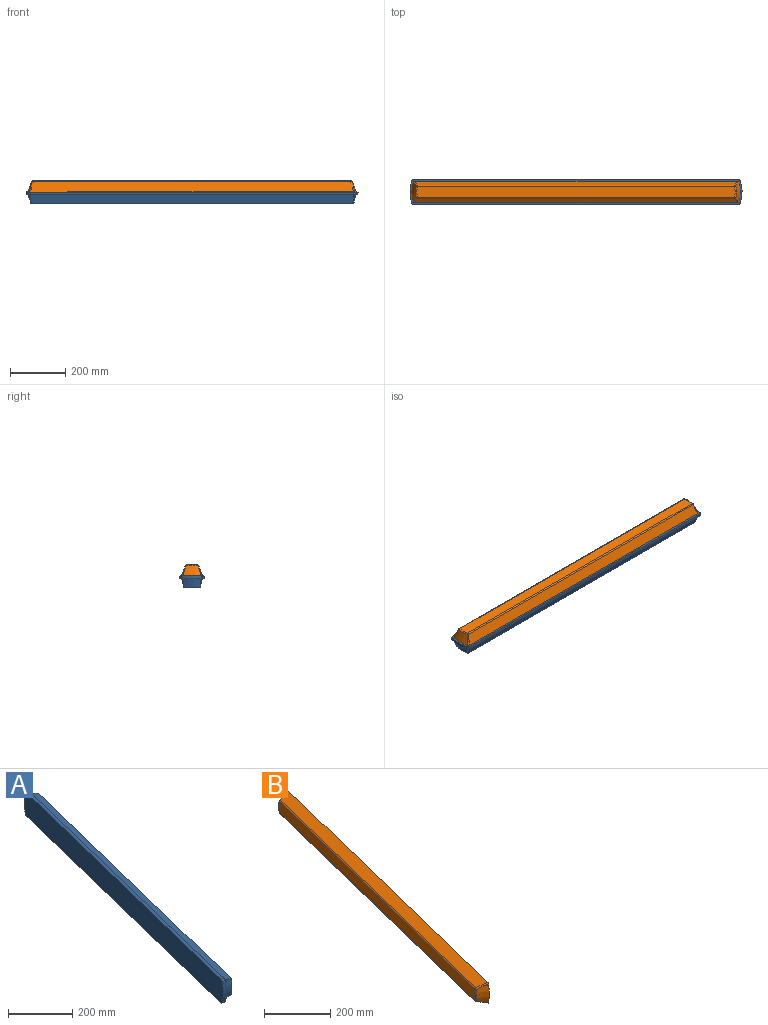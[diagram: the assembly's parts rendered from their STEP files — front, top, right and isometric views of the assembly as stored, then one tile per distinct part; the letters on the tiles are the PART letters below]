
ASSEMBLY  parts=2 mates=1
PART A: 27 faces, bbox 325.7x1167.6x90 mm
  f0: plane 1165.2x290.52mm, normal (0.97,-0.24,0), area 17663.3mm2, adj f1,f2,f3,f4,f5,f6,f7,f8
  f1: cylinder r=10mm len=12.04mm, axis (-0.97,0.24,0), area 130.5mm2, adj f0,f2,f12,f13
  f2: plane 10.02x4.74mm, normal (0.23,0.94,-0.26), area 49.1mm2, adj f0,f1,f3,f13
  f3: cylinder r=125mm len=65.78mm, axis (-0.97,0.24,0), area 665.7mm2, adj f0,f2,f4,f13
  f4: plane 10.02x4.74mm, normal (0.23,0.94,0.26), area 49.1mm2, adj f0,f3,f5,f13
  f5: cylinder r=10mm len=12.04mm, axis (-0.97,0.24,0), area 130.5mm2, adj f0,f4,f6,f13
  f6: plane 1137.84x292.79mm, normal (0,0,1), area 11701.8mm2, adj f0,f5,f7,f13
  f7: cylinder r=10mm len=12.04mm, axis (-0.97,0.24,0), area 130.5mm2, adj f0,f6,f8,f13
  f8: plane 10.02x4.74mm, normal (-0.23,-0.94,0.26), area 49.1mm2, adj f0,f7,f9,f13
  f9: cylinder r=125mm len=65.78mm, axis (-0.97,0.24,0), area 665.7mm2, adj f0,f8,f10,f13
  f10: plane 10.02x4.74mm, normal (-0.23,-0.94,-0.26), area 49.1mm2, adj f0,f9,f11,f13
  f11: cylinder r=10mm len=12.04mm, axis (-0.97,0.24,0), area 130.5mm2, adj f0,f10,f12,f13
  f12: plane 1137.84x292.79mm, normal (0,0,-1), area 11701.8mm2, adj f0,f1,f11,f13
  f13: plane 1165.2x290.52mm, normal (-0.97,0.24,0), area 107548.4mm2, adj f1,f2,f3,f4,f5,f6,f7,f8
  f14: plane 1138.94x311.27mm, normal (0.25,-0.06,-0.97), area 36268.8mm2, adj f0,f15,f16,f24,f25,f26
  f15: cone r=0.3mm half-angle=15deg, axis (-0.97,0.24,0), area 22.7mm2, adj f0,f14,f16
  f16: plane 27.55x15.05mm, normal (0.48,0.84,-0.25), area 115.1mm2, adj f0,f14,f15,f17,f26
  f17: cone r=110.77mm half-angle=15deg, axis (-0.97,0.24,0), area 1885.2mm2, adj f0,f16,f18,f26
  f18: plane 27.55x15.05mm, normal (0.48,0.84,0.25), area 115.1mm2, adj f0,f17,f19,f20,f26
  f19: cone r=0.3mm half-angle=15deg, axis (-0.97,0.24,0), area 22.7mm2, adj f0,f18,f20
  f20: plane 1138.94x311.27mm, normal (0.25,-0.06,0.97), area 36268.8mm2, adj f0,f18,f19,f21,f22,f26
  f21: cone r=0.3mm half-angle=15deg, axis (-0.97,0.24,0), area 22.7mm2, adj f0,f20,f22
  f22: plane 31.05x6.85mm, normal (0.03,-0.97,0.25), area 115.1mm2, adj f0,f20,f21,f23,f26
  f23: cone r=110.77mm half-angle=15deg, axis (-0.97,0.24,0), area 1885.2mm2, adj f0,f22,f24,f26
  f24: plane 31.05x6.85mm, normal (0.03,-0.97,-0.25), area 115.1mm2, adj f0,f14,f23,f25,f26
  f25: cone r=0.3mm half-angle=15deg, axis (-0.97,0.24,0), area 22.7mm2, adj f0,f14,f24
  f26: plane 1136.01x283.24mm, normal (0.97,-0.24,0), area 69992.4mm2, adj f14,f16,f17,f18,f20,f22,f23,f24
PART B: 26 faces, bbox 324.4x1156.6x76.8 mm
  f0: sphere r=5mm, area 17.3mm2, adj f8,f11,f13
  f1: sphere r=5mm, area 17.3mm2, adj f6,f10,f11
  f2: sphere r=5mm, area 17.3mm2, adj f4,f7,f8
  f3: sphere r=5mm, area 17.3mm2, adj f4,f5,f6
  f4: cylinder r=5mm len=1113.46mm, axis (0.24,0.97,0), area 7005mm2, adj f2,f3,f21,f22
  f5: bspline ~25.75x12.39mm, area 162.6mm2, adj f3,f9,f22,f24
  f6: torus R=99.94mm, axis (0.97,-0.24,0), area 251.9mm2, adj f1,f3,f21,f24
  f7: bspline ~22.68x16.74mm, area 162.6mm2, adj f2,f12,f17,f22
  f8: torus R=99.94mm, axis (0.97,-0.24,0), area 251.9mm2, adj f0,f2,f17,f21
  f9: cylinder r=5mm len=14.59mm, axis (0.94,0.03,-0.33), area 86.8mm2, adj f5,f20,f22,f25
  f10: bspline ~25.75x12.39mm, area 162.6mm2, adj f1,f14,f19,f24
  f11: cylinder r=5mm len=1113.46mm, axis (-0.24,-0.97,0), area 7005mm2, adj f0,f1,f19,f21
  f12: cylinder r=5mm len=12.94mm, axis (0.82,-0.47,-0.33), area 86.8mm2, adj f7,f16,f20,f22
  f13: bspline ~22.68x16.74mm, area 162.6mm2, adj f0,f15,f17,f19
  f14: cylinder r=5mm len=14.59mm, axis (0.94,0.03,0.33), area 86.8mm2, adj f10,f19,f20,f23
  f15: cylinder r=5mm len=12.94mm, axis (0.82,-0.47,0.33), area 86.8mm2, adj f13,f18,f19,f20
  f16: plane 11.74x7.58mm, normal (-0.55,-0.8,-0.25), area 25mm2, adj f12,f17,f20
  f17: cone r=105.97mm half-angle=20deg, axis (0.97,-0.24,0), area 2138.5mm2, adj f7,f8,f13,f16,f18,f20
  f18: plane 11.74x7.58mm, normal (-0.55,-0.8,0.25), area 25mm2, adj f15,f17,f20
  f19: plane 1132.9x315.56mm, normal (-0.33,0.08,0.94), area 45210.5mm2, adj f10,f11,f13,f14,f15,f20
  f20: plane 1152.43x287.95mm, normal (0.97,-0.24,0), area 89879.5mm2, adj f9,f12,f14,f15,f16,f17,f18,f19
  f21: plane 1116.57x278.39mm, normal (-0.97,0.24,0), area 45839mm2, adj f4,f6,f8,f11
  f22: plane 1132.9x315.56mm, normal (-0.33,0.08,-0.94), area 45210.5mm2, adj f4,f5,f7,f9,f12,f20
  f23: plane 13.72x4.73mm, normal (-0.11,0.96,0.25), area 25mm2, adj f14,f20,f24
  f24: cone r=105.97mm half-angle=20deg, axis (0.97,-0.24,0), area 2138.5mm2, adj f5,f6,f10,f20,f23,f25
  f25: plane 13.72x4.73mm, normal (-0.11,0.96,-0.25), area 25mm2, adj f9,f20,f24
PLACE A rot(axis=(0.67,0.52,-0.52),112.3deg) t=(-187.23,-13279.11,5351.09)mm
PLACE B rot(axis=(0.67,0.52,-0.52),112.3deg) t=(-187.23,-13279.11,5351.09)mm
MATE fastened B.f20 <-> A.f13  axis (0,0,-1) through (0,0,40)mm
